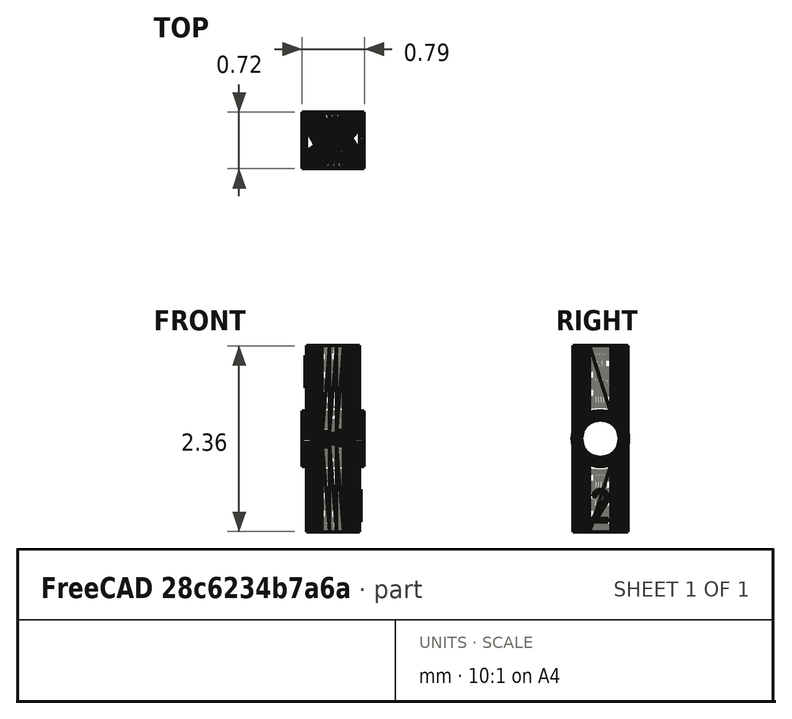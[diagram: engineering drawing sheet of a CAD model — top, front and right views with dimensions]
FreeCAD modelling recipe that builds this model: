
FCSTD DOCUMENT  (FreeCAD 0.20R29177 +426 (Git))
Label: pin connector
License: All rights reserved
LicenseURL: https://en.wikipedia.org/wiki/All_rights_reserved
objects: Part::Feature×82, Mesh::Feature×42, Part::Refine×41, Part::MultiFuse×1
note: 124 computed .brp shape members not serialized (recipe doc carries the construction recipe); baked Part::Feature solids carry a one-line shape summary decoded from their .brp

FEATURE [Part::Feature] Component041_solid  label="Component041 (Solid)"
  shape: bbox 0.79 x 0.717 x 0.71 mm, 768 faces (baked)
FEATURE [Part::Feature] Component001001_solid  label="Component001001 (Solid)"
  shape: bbox 0.6715 x 0.695 x 0.7889 mm, 332 faces (baked)
FEATURE [Part::Feature] Component002001_solid  label="Component002001 (Solid)"
  shape: bbox 0.6715 x 0.695 x 0.7889 mm, 332 faces (baked)
FEATURE [Part::Feature] Component003001_solid  label="Component003001 (Solid)"
  shape: bbox 0.474 x 0.478 x 2.596e-07 mm, 48 faces (baked)
FEATURE [Part::Feature] Component004001_solid  label="Component004001 (Solid)"
  shape: bbox 0.474 x 0.478 x 2.596e-07 mm, 48 faces (baked)
FEATURE [Part::Feature] Component005001_solid  label="Component005001 (Solid)"
  shape: bbox 0.1997 x 0.2014 x 1.087 mm, 35 faces (baked)
FEATURE [Part::Feature] Component006001_solid  label="Component006001 (Solid)"
  shape: bbox 0.1997 x 0.2014 x 1.087 mm, 35 faces (baked)
FEATURE [Part::Feature] Component007001_solid  label="Component007001 (Solid)"
  shape: bbox 0.1997 x 0.2014 x 1.087 mm, 35 faces (baked)
FEATURE [Part::Feature] Component008001_solid  label="Component008001 (Solid)"
  shape: bbox 0.1997 x 0.2014 x 1.087 mm, 35 faces (baked)
FEATURE [Part::Feature] Component009001_solid  label="Component009001 (Solid)"
  shape: bbox 0.1997 x 0.2014 x 1.087 mm, 35 faces (baked)
FEATURE [Part::Feature] Component010001_solid  label="Component010001 (Solid)"
  shape: bbox 0.1997 x 0.2014 x 1.087 mm, 35 faces (baked)
FEATURE [Part::Feature] Component011001_solid  label="Component011001 (Solid)"
  shape: bbox 0.1997 x 0.2014 x 1.087 mm, 35 faces (baked)
FEATURE [Part::Feature] Component012001_solid  label="Component012001 (Solid)"
  shape: bbox 0.1997 x 0.2014 x 1.087 mm, 35 faces (baked)
FEATURE [Part::Feature] Component013001_solid  label="Component013001 (Solid)"
  shape: bbox 0.01975 x 0.2041 x 0.4092 mm, 29 faces (baked)
FEATURE [Part::Feature] Component014001_solid  label="Component014001 (Solid)"
  shape: bbox 0.01975 x 0.2041 x 0.4092 mm, 29 faces (baked)
FEATURE [Part::Feature] Component015001_solid  label="Component015001 (Solid)"
  shape: bbox 0.01975 x 0.06971 x 0.09368 mm, 8 faces (baked)
FEATURE [Part::Feature] Component016001_solid  label="Component016001 (Solid)"
  shape: bbox 0.01975 x 0.06971 x 0.09368 mm, 8 faces (baked)
FEATURE [Part::Feature] Component017001_solid  label="Component017001 (Solid)"
  shape: bbox 0.2721 x 0.008962 x 1.129 mm, 6 faces (baked)
FEATURE [Part::Feature] Component018001_solid  label="Component018001 (Solid)"
  shape: bbox 0.2721 x 0.008962 x 1.129 mm, 6 faces (baked)
FEATURE [Part::Feature] Component019001_solid  label="Component019001 (Solid)"
  shape: bbox 0.2721 x 0.008962 x 1.129 mm, 6 faces (baked)
FEATURE [Part::Feature] Component020001_solid  label="Component020001 (Solid)"
  shape: bbox 0.2721 x 0.008962 x 1.129 mm, 6 faces (baked)
FEATURE [Part::Feature] Component021001_solid  label="Component021001 (Solid)"
  shape: bbox 0.01975 x 0.1593 x 0.286 mm, 4 faces (baked)
FEATURE [Part::Feature] Component022001_solid  label="Component022001 (Solid)"
  shape: bbox 0.01975 x 0.1593 x 0.286 mm, 4 faces (baked)
FEATURE [Part::Feature] Component023001_solid  label="Component023001 (Solid)"
  shape: bbox 2e-07 x 0.2744 x 0.8554 mm, 2 faces (baked)
FEATURE [Part::Feature] Component024001_solid  label="Component024001 (Solid)"
  shape: bbox 2e-07 x 0.2744 x 0.8554 mm, 2 faces (baked)
FEATURE [Part::Feature] Component025001_solid  label="Component025001 (Solid)"
  shape: bbox 2e-07 x 0.2744 x 0.8554 mm, 2 faces (baked)
FEATURE [Part::Feature] Component026001_solid  label="Component026001 (Solid)"
  shape: bbox 2e-07 x 0.2744 x 0.8554 mm, 2 faces (baked)
FEATURE [Part::Feature] Component027001_solid  label="Component027001 (Solid)"
  shape: bbox 0.01975 x 0.04481 x 0.02465 mm, 2 faces (baked)
FEATURE [Part::Feature] Component028001_solid  label="Component028001 (Solid)"
  shape: bbox 0.01975 x 0.02988 x 0.01479 mm, 2 faces (baked)
FEATURE [Part::Feature] Component029001_solid  label="Component029001 (Solid)"
  shape: bbox 0.01975 x 0.1494 x 0.2416 mm, 2 faces (baked)
FEATURE [Part::Feature] Component030001_solid  label="Component030001 (Solid)"
  shape: bbox 0.01975 x 0.004979 x 0.05917 mm, 2 faces (baked)
FEATURE [Part::Feature] Component031001_solid  label="Component031001 (Solid)"
  shape: bbox 0.01975 x 0.02988 x 0.04438 mm, 2 faces (baked)
FEATURE [Part::Feature] Component032001_solid  label="Component032001 (Solid)"
  shape: bbox 0.01975 x 0.05477 x 2e-07 mm, 2 faces (baked)
FEATURE [Part::Feature] Component033001_solid  label="Component033001 (Solid)"
  shape: bbox 0.01975 x 0.1942 x 2e-07 mm, 2 faces (baked)
FEATURE [Part::Feature] Component034001_solid  label="Component034001 (Solid)"
  shape: bbox 0.01975 x 0.04481 x 0.02465 mm, 2 faces (baked)
FEATURE [Part::Feature] Component035001_solid  label="Component035001 (Solid)"
  shape: bbox 0.01975 x 0.02988 x 0.01479 mm, 2 faces (baked)
FEATURE [Part::Feature] Component036001_solid  label="Component036001 (Solid)"
  shape: bbox 0.01975 x 0.1494 x 0.2416 mm, 2 faces (baked)
FEATURE [Part::Feature] Component037001_solid  label="Component037001 (Solid)"
  shape: bbox 0.01975 x 0.004979 x 0.05917 mm, 2 faces (baked)
FEATURE [Part::Feature] Component038001_solid  label="Component038001 (Solid)"
  shape: bbox 0.01975 x 0.02988 x 0.04438 mm, 2 faces (baked)
FEATURE [Part::Feature] Component039001_solid  label="Component039001 (Solid)"
  shape: bbox 0.01975 x 0.05477 x 2e-07 mm, 2 faces (baked)
FEATURE [Part::Feature] Component040001_solid  label="Component040001 (Solid)"
  shape: bbox 0.01975 x 0.1942 x 2e-07 mm, 2 faces (baked)
FEATURE [Part::Refine] Component041_solid001  label="Component041 (Solid)001"
  Source = -> Component041_solid
FEATURE [Part::Refine] Component001001_solid001  label="Component001001 (Solid)001"
  Source = -> Component001001_solid
FEATURE [Part::Refine] Component002001_solid001  label="Component002001 (Solid)001"
  Source = -> Component002001_solid
FEATURE [Part::Refine] Component003001_solid001  label="Component003001 (Solid)001"
  Source = -> Component003001_solid
FEATURE [Part::Refine] Component004001_solid001  label="Component004001 (Solid)001"
  Source = -> Component004001_solid
FEATURE [Part::Refine] Component005001_solid001  label="Component005001 (Solid)001"
  Source = -> Component005001_solid
FEATURE [Part::Refine] Component006001_solid001  label="Component006001 (Solid)001"
  Source = -> Component006001_solid
FEATURE [Part::Refine] Component007001_solid001  label="Component007001 (Solid)001"
  Source = -> Component007001_solid
FEATURE [Part::Refine] Component008001_solid001  label="Component008001 (Solid)001"
  Source = -> Component008001_solid
FEATURE [Part::Refine] Component009001_solid001  label="Component009001 (Solid)001"
  Source = -> Component009001_solid
FEATURE [Part::Refine] Component010001_solid001  label="Component010001 (Solid)001"
  Source = -> Component010001_solid
FEATURE [Part::Refine] Component011001_solid001  label="Component011001 (Solid)001"
  Source = -> Component011001_solid
FEATURE [Part::Refine] Component012001_solid001  label="Component012001 (Solid)001"
  Source = -> Component012001_solid
FEATURE [Part::Refine] Component013001_solid001  label="Component013001 (Solid)001"
  Source = -> Component013001_solid
FEATURE [Part::Refine] Component014001_solid001  label="Component014001 (Solid)001"
  Source = -> Component014001_solid
FEATURE [Part::Refine] Component015001_solid001  label="Component015001 (Solid)001"
  Source = -> Component015001_solid
FEATURE [Part::Refine] Component016001_solid001  label="Component016001 (Solid)001"
  Source = -> Component016001_solid
FEATURE [Part::Refine] Component017001_solid001  label="Component017001 (Solid)001"
  Source = -> Component017001_solid
FEATURE [Part::Refine] Component018001_solid001  label="Component018001 (Solid)001"
  Source = -> Component018001_solid
FEATURE [Part::Refine] Component019001_solid001  label="Component019001 (Solid)001"
  Source = -> Component019001_solid
FEATURE [Part::Refine] Component020001_solid001  label="Component020001 (Solid)001"
  Source = -> Component020001_solid
FEATURE [Part::Refine] Component021001_solid001  label="Component021001 (Solid)001"
  Source = -> Component021001_solid
FEATURE [Part::Refine] Component022001_solid001  label="Component022001 (Solid)001"
  Source = -> Component022001_solid
FEATURE [Part::Refine] Component023001_solid001  label="Component023001 (Solid)001"
  Source = -> Component023001_solid
FEATURE [Part::Refine] Component024001_solid001  label="Component024001 (Solid)001"
  Source = -> Component024001_solid
FEATURE [Part::Refine] Component025001_solid001  label="Component025001 (Solid)001"
  Source = -> Component025001_solid
FEATURE [Part::Refine] Component026001_solid001  label="Component026001 (Solid)001"
  Source = -> Component026001_solid
FEATURE [Part::Refine] Component027001_solid001  label="Component027001 (Solid)001"
  Source = -> Component027001_solid
FEATURE [Part::Refine] Component028001_solid001  label="Component028001 (Solid)001"
  Source = -> Component028001_solid
FEATURE [Part::Refine] Component029001_solid001  label="Component029001 (Solid)001"
  Source = -> Component029001_solid
FEATURE [Part::Refine] Component030001_solid001  label="Component030001 (Solid)001"
  Source = -> Component030001_solid
FEATURE [Part::Refine] Component031001_solid001  label="Component031001 (Solid)001"
  Source = -> Component031001_solid
FEATURE [Part::Refine] Component032001_solid001  label="Component032001 (Solid)001"
  Source = -> Component032001_solid
FEATURE [Part::Refine] Component033001_solid001  label="Component033001 (Solid)001"
  Source = -> Component033001_solid
FEATURE [Part::Refine] Component034001_solid001  label="Component034001 (Solid)001"
  Source = -> Component034001_solid
FEATURE [Part::Refine] Component035001_solid001  label="Component035001 (Solid)001"
  Source = -> Component035001_solid
FEATURE [Part::Refine] Component036001_solid001  label="Component036001 (Solid)001"
  Source = -> Component036001_solid
FEATURE [Part::Refine] Component037001_solid001  label="Component037001 (Solid)001"
  Source = -> Component037001_solid
FEATURE [Part::Refine] Component038001_solid001  label="Component038001 (Solid)001"
  Source = -> Component038001_solid
FEATURE [Part::Refine] Component039001_solid001  label="Component039001 (Solid)001"
  Source = -> Component039001_solid
FEATURE [Part::Refine] Component040001_solid001  label="Component040001 (Solid)001"
  Source = -> Component040001_solid
FEATURE [Part::MultiFuse] Fusion
  Refine = true
  Shapes = -> [Component041_solid001,Component001001_solid001,Component002001_solid001,Component003001_solid001,Component004001_solid001,Component005001_solid001,Component006001_solid001,Component007001_solid001,Component008001_solid001,Component009001_solid001,Component010001_solid001,Component011001_solid001,Component012001_solid001,Component013001_solid001,Component014001_solid001,Component015001_solid001,+25 more]
FEATURE [Part::Feature] Component040001
  shape: bbox 0.01975 x 0.1942 x 2e-07 mm, 2 faces, 0 solids (baked)
FEATURE [Mesh::Feature] Axle_and_Pin_Connector__Angled__2___180_degrees  label="Axle and Pin Connector, Angled #2 - 180 degrees"
FEATURE [Mesh::Feature] Component
FEATURE [Mesh::Feature] Component001 .. Component040  x40 (patterned run collapsed; names and placements below)
FEATURE [Part::Feature] Component041
  shape: bbox 0.79 x 0.717 x 0.71 mm, 768 faces, 0 solids (baked)
FEATURE [Part::Feature] Component001001
  shape: bbox 0.6715 x 0.695 x 0.7889 mm, 332 faces, 0 solids (baked)
FEATURE [Part::Feature] Component002001
  shape: bbox 0.6715 x 0.695 x 0.7889 mm, 332 faces, 0 solids (baked)
FEATURE [Part::Feature] Component003001
  shape: bbox 0.474 x 0.478 x 2.596e-07 mm, 48 faces, 0 solids (baked)
FEATURE [Part::Feature] Component004001
  shape: bbox 0.474 x 0.478 x 2.596e-07 mm, 48 faces, 0 solids (baked)
FEATURE [Part::Feature] Component005001
  shape: bbox 0.1997 x 0.2014 x 1.087 mm, 35 faces, 0 solids (baked)
FEATURE [Part::Feature] Component006001
  shape: bbox 0.1997 x 0.2014 x 1.087 mm, 35 faces, 0 solids (baked)
FEATURE [Part::Feature] Component007001
  shape: bbox 0.1997 x 0.2014 x 1.087 mm, 35 faces, 0 solids (baked)
FEATURE [Part::Feature] Component008001
  shape: bbox 0.1997 x 0.2014 x 1.087 mm, 35 faces, 0 solids (baked)
FEATURE [Part::Feature] Component009001
  shape: bbox 0.1997 x 0.2014 x 1.087 mm, 35 faces, 0 solids (baked)
FEATURE [Part::Feature] Component010001
  shape: bbox 0.1997 x 0.2014 x 1.087 mm, 35 faces, 0 solids (baked)
FEATURE [Part::Feature] Component011001
  shape: bbox 0.1997 x 0.2014 x 1.087 mm, 35 faces, 0 solids (baked)
FEATURE [Part::Feature] Component012001
  shape: bbox 0.1997 x 0.2014 x 1.087 mm, 35 faces, 0 solids (baked)
FEATURE [Part::Feature] Component013001
  shape: bbox 0.01975 x 0.2041 x 0.4092 mm, 29 faces, 0 solids (baked)
FEATURE [Part::Feature] Component014001
  shape: bbox 0.01975 x 0.2041 x 0.4092 mm, 29 faces, 0 solids (baked)
FEATURE [Part::Feature] Component015001
  shape: bbox 0.01975 x 0.06971 x 0.09368 mm, 8 faces, 0 solids (baked)
FEATURE [Part::Feature] Component016001
  shape: bbox 0.01975 x 0.06971 x 0.09368 mm, 8 faces, 0 solids (baked)
FEATURE [Part::Feature] Component017001
  shape: bbox 0.2721 x 0.008962 x 1.129 mm, 6 faces, 0 solids (baked)
FEATURE [Part::Feature] Component018001
  shape: bbox 0.2721 x 0.008962 x 1.129 mm, 6 faces, 0 solids (baked)
FEATURE [Part::Feature] Component019001
  shape: bbox 0.2721 x 0.008962 x 1.129 mm, 6 faces, 0 solids (baked)
FEATURE [Part::Feature] Component020001
  shape: bbox 0.2721 x 0.008962 x 1.129 mm, 6 faces, 0 solids (baked)
FEATURE [Part::Feature] Component021001
  shape: bbox 0.01975 x 0.1593 x 0.286 mm, 4 faces, 0 solids (baked)
FEATURE [Part::Feature] Component022001
  shape: bbox 0.01975 x 0.1593 x 0.286 mm, 4 faces, 0 solids (baked)
FEATURE [Part::Feature] Component023001
  shape: bbox 2e-07 x 0.2744 x 0.8554 mm, 2 faces, 0 solids (baked)
FEATURE [Part::Feature] Component024001
  shape: bbox 2e-07 x 0.2744 x 0.8554 mm, 2 faces, 0 solids (baked)
FEATURE [Part::Feature] Component025001
  shape: bbox 2e-07 x 0.2744 x 0.8554 mm, 2 faces, 0 solids (baked)
FEATURE [Part::Feature] Component026001
  shape: bbox 2e-07 x 0.2744 x 0.8554 mm, 2 faces, 0 solids (baked)
FEATURE [Part::Feature] Component027001
  shape: bbox 0.01975 x 0.04481 x 0.02465 mm, 2 faces, 0 solids (baked)
FEATURE [Part::Feature] Component028001
  shape: bbox 0.01975 x 0.02988 x 0.01479 mm, 2 faces, 0 solids (baked)
FEATURE [Part::Feature] Component029001
  shape: bbox 0.01975 x 0.1494 x 0.2416 mm, 2 faces, 0 solids (baked)
FEATURE [Part::Feature] Component030001
  shape: bbox 0.01975 x 0.004979 x 0.05917 mm, 2 faces, 0 solids (baked)
FEATURE [Part::Feature] Component031001
  shape: bbox 0.01975 x 0.02988 x 0.04438 mm, 2 faces, 0 solids (baked)
FEATURE [Part::Feature] Component032001
  shape: bbox 0.01975 x 0.05477 x 2e-07 mm, 2 faces, 0 solids (baked)
FEATURE [Part::Feature] Component033001
  shape: bbox 0.01975 x 0.1942 x 2e-07 mm, 2 faces, 0 solids (baked)
FEATURE [Part::Feature] Component034001
  shape: bbox 0.01975 x 0.04481 x 0.02465 mm, 2 faces, 0 solids (baked)
FEATURE [Part::Feature] Component035001
  shape: bbox 0.01975 x 0.02988 x 0.01479 mm, 2 faces, 0 solids (baked)
FEATURE [Part::Feature] Component036001
  shape: bbox 0.01975 x 0.1494 x 0.2416 mm, 2 faces, 0 solids (baked)
FEATURE [Part::Feature] Component037001
  shape: bbox 0.01975 x 0.004979 x 0.05917 mm, 2 faces, 0 solids (baked)
FEATURE [Part::Feature] Component038001
  shape: bbox 0.01975 x 0.02988 x 0.04438 mm, 2 faces, 0 solids (baked)
FEATURE [Part::Feature] Component039001
  shape: bbox 0.01975 x 0.05477 x 2e-07 mm, 2 faces, 0 solids (baked)
